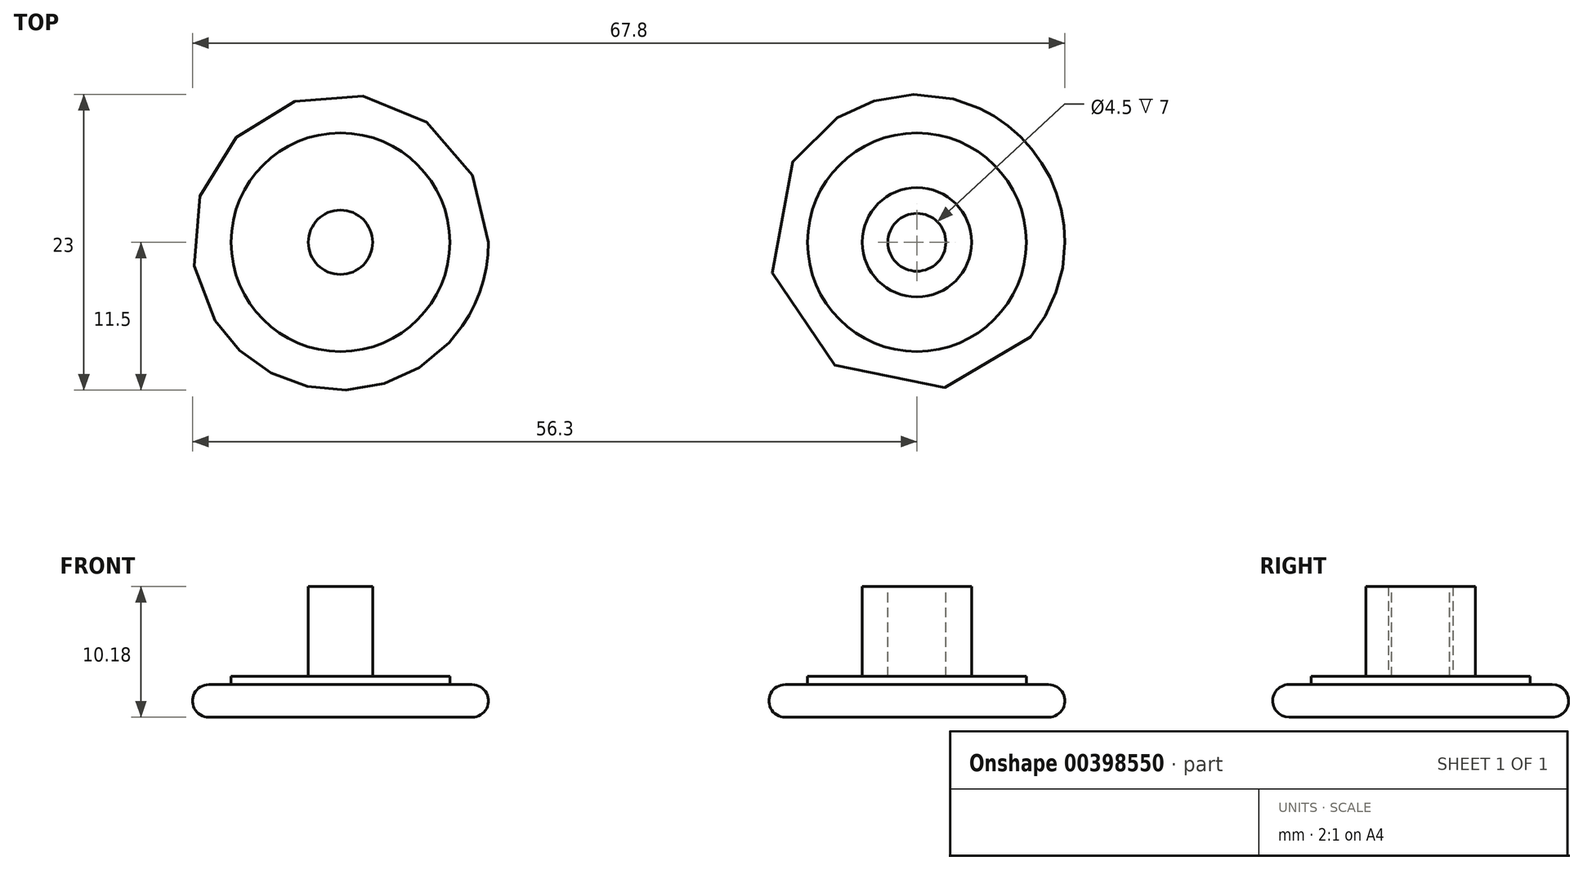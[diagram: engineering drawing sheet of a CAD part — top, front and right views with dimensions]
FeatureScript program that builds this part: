
annotation { "Feature Type Name" : "Feature", "Feature Type Description" : "" }
export const myFeature = defineFeature(function(context is Context, id is Id, definition is map)
    precondition{}
    {
        {
            var Q0;
            Q0=qCreatedBy(makeId("Top.planeOp"),FACE);
            var sketch = newSketch(context, id + "F0", { "sketchPlane" : qUnion([Q0])});
            skCircle(sketch, "E0", {"center": v(0, 0) * mm, "radius": 11.5 * mm});
            skCircle(sketch, "E1", {"center": v(0, 0) * mm, "radius": 4.25 * mm});
            skCircle(sketch, "E2", {"center": v(0, 0) * mm, "radius": 8.5 * mm});
            skSolve(sketch);
        }
        {
            var Q0;
            Q0=makeQuery(id+"F0.imprint","IMPRINT",FACE,{"disambiguationData":[TD([[makeQuery(id+"F0.imprint","IMPRINT",EDGE,{"derivedFrom":sQuery(id+"F0.wireOp",EDGE,"E0")}),1.0]])]});
            extrude(context, id + "F1", {"entities" : qUnion([Q0]), "depth" : 2.54 * mm});
        }
        {
            var Q0;
            Q0=makeQuery(id+"F0.imprint","IMPRINT",FACE,{"disambiguationData":[TD([[makeQuery(id+"F0.imprint","IMPRINT",EDGE,{"derivedFrom":sQuery(id+"F0.wireOp",EDGE,"E1")}),-1.0]])]});
            extrude(context, id + "F2", {"entities" : qUnion([Q0]), "operationType" : NewBodyOperationType.ADD, "depth" : 3.17 * mm});
        }
        {
            var Q0;
            Q0=makeQuery(id+"F0.imprint","IMPRINT",FACE,{"disambiguationData":[TD([[makeQuery(id+"F0.imprint","IMPRINT",EDGE,{"derivedFrom":sQuery(id+"F0.wireOp",EDGE,"E1")}),1.0]])]});
            extrude(context, id + "F3", {"entities" : qUnion([Q0]), "operationType" : NewBodyOperationType.ADD, "depth" : 7 * mm + 3.17 * mm});
        }
        {
            var Q0;
            Q0=makeQuery(id+"F1.opExtrude","CAP_EDGE",EDGE,{"disambiguationData":[OSD([sQuery(id+"F0.wireOp",EDGE,"E0")])],"isStart":false});
            var Q1;
            Q1=makeQuery(id+"F1.opExtrude","CAP_EDGE",EDGE,{"disambiguationData":[OSD([sQuery(id+"F0.wireOp",EDGE,"E0")])],"isStart":true});
            fillet(context, id + "F4", {"entities" : qUnion([Q0, Q1]), "radius" : 1.27 * mm, "tangentPropagation" : true, "allowEdgeOverflow" : false});
        }
        {
            var Q0;
            Q0=qCreatedBy(makeId("Top.planeOp"),FACE);
            var sketch = newSketch(context, id + "F5", { "sketchPlane" : qUnion([Q0])});
            skCircle(sketch, "E3", {"center": v(-44.8, 0) * mm, "radius": 11.5 * mm});
            skCircle(sketch, "E4", {"center": v(-44.8, 0) * mm, "radius": 8.5 * mm});
            skCircle(sketch, "E5", {"center": v(-44.8, 0) * mm, "radius": 2.5 * mm});
            skSolve(sketch);
        }
        {
            var Q0;
            Q0=makeQuery(id+"F5.imprint","IMPRINT",FACE,{"disambiguationData":[TD([[makeQuery(id+"F5.imprint","IMPRINT",EDGE,{"derivedFrom":sQuery(id+"F5.wireOp",EDGE,"E3")}),1.0]])]});
            extrude(context, id + "F6", {"entities" : qUnion([Q0]), "depth" : 2.54 * mm});
        }
        {
            var Q0;
            Q0=makeQuery(id+"F5.imprint","IMPRINT",FACE,{"disambiguationData":[TD([[makeQuery(id+"F5.imprint","IMPRINT",EDGE,{"derivedFrom":sQuery(id+"F5.wireOp",EDGE,"E4")}),1.0]])]});
            extrude(context, id + "F7", {"entities" : qUnion([Q0]), "operationType" : NewBodyOperationType.ADD, "depth" : 3.17 * mm});
        }
        {
            var Q0;
            Q0=makeQuery(id+"F5.imprint","IMPRINT",FACE,{"disambiguationData":[TD([[makeQuery(id+"F5.imprint","IMPRINT",EDGE,{"derivedFrom":sQuery(id+"F5.wireOp",EDGE,"E5")}),1.0]])]});
            extrude(context, id + "F8", {"entities" : qUnion([Q0]), "operationType" : NewBodyOperationType.ADD, "depth" : 7 * mm + 3.17 * mm});
        }
        {
            var Q0;
            Q0=makeQuery(id+"F3.opExtrude","CAP_FACE",FACE,{"disambiguationData":[OSD([sQuery(id+"F0.wireOp",EDGE,"E1")])],"isStart":false});
            var sketch = newSketch(context, id + "F9", { "sketchPlane" : qUnion([Q0])});
            skCircle(sketch, "E6", {"center": v(0, 0) * mm, "radius": 2.25 * mm});
            skSolve(sketch);
        }
        {
            var Q0;
            Q0=makeQuery(id+"F9.imprint","IMPRINT",FACE,{"disambiguationData":[TD([[makeQuery(id+"F9.imprint","IMPRINT",EDGE,{"derivedFrom":sQuery(id+"F9.wireOp",EDGE,"E6")}),1.0]])]});
            extrude(context, id + "F10", {"entities" : qUnion([Q0]), "operationType" : NewBodyOperationType.REMOVE, "oppositeDirection" : true, "depth" : 7 * mm});
        }
        {
            var Q0;
            Q0=makeQuery(id+"F6.opExtrude","CAP_EDGE",EDGE,{"disambiguationData":[OSD([sQuery(id+"F5.wireOp",EDGE,"E3")])],"isStart":false});
            var Q1;
            Q1=makeQuery(id+"F6.opExtrude","CAP_EDGE",EDGE,{"disambiguationData":[OSD([sQuery(id+"F5.wireOp",EDGE,"E3")])],"isStart":true});
            fillet(context, id + "F11", {"entities" : qUnion([Q0, Q1]), "radius" : 1.27 * mm, "tangentPropagation" : true, "allowEdgeOverflow" : false});
        }
    });
